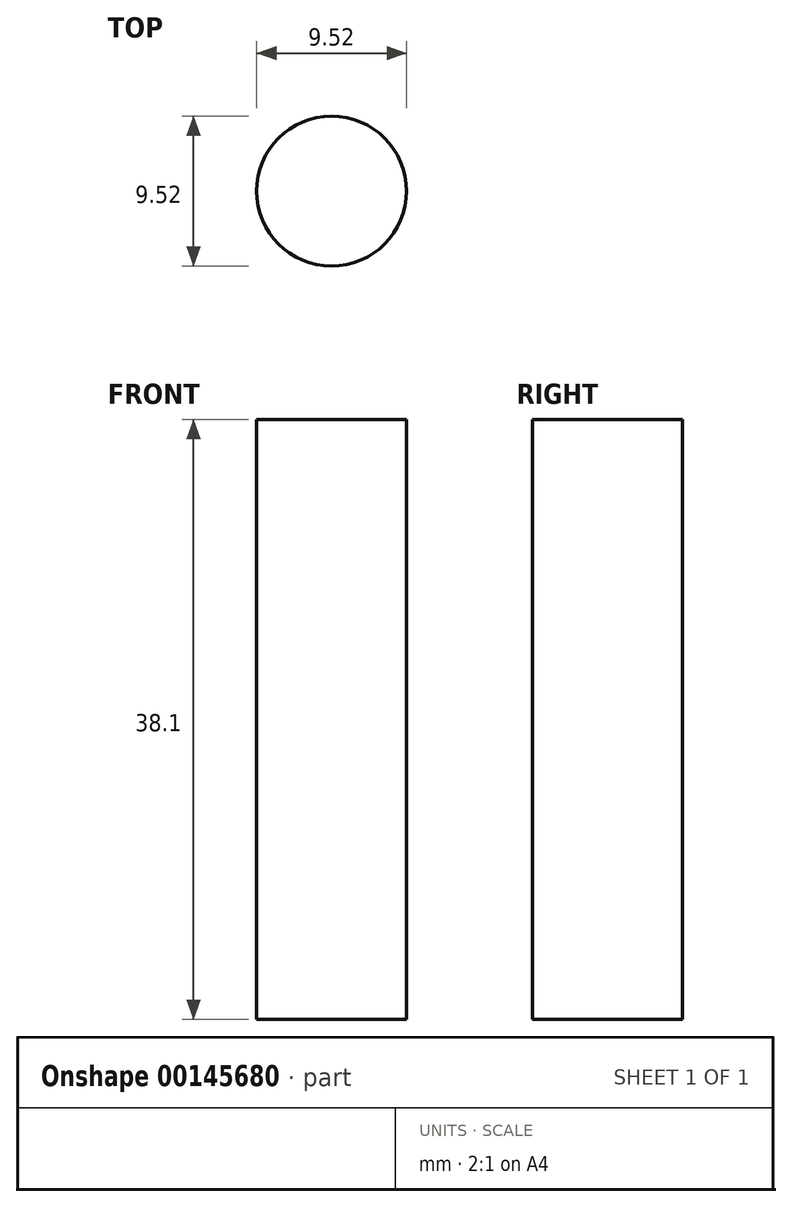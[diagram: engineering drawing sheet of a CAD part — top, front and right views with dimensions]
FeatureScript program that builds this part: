
annotation { "Feature Type Name" : "Feature", "Feature Type Description" : "" }
export const myFeature = defineFeature(function(context is Context, id is Id, definition is map)
    precondition{}
    {
        {
            var Q0;
            Q0=qCreatedBy(makeId("Top.planeOp"),FACE);
            var sketch = newSketch(context, id + "F0", { "sketchPlane" : qUnion([Q0])});
            skCircle(sketch, "E0", {"center": v(0, 0) * mm, "radius": 4.76 * mm});
            skSolve(sketch);
        }
        {
            var Q0;
            Q0 = qSketchRegion(id + "F0", true);
            extrude(context, id + "F1", {"entities" : qUnion([Q0]), "depth" : 38.1 * mm});
        }
    });
